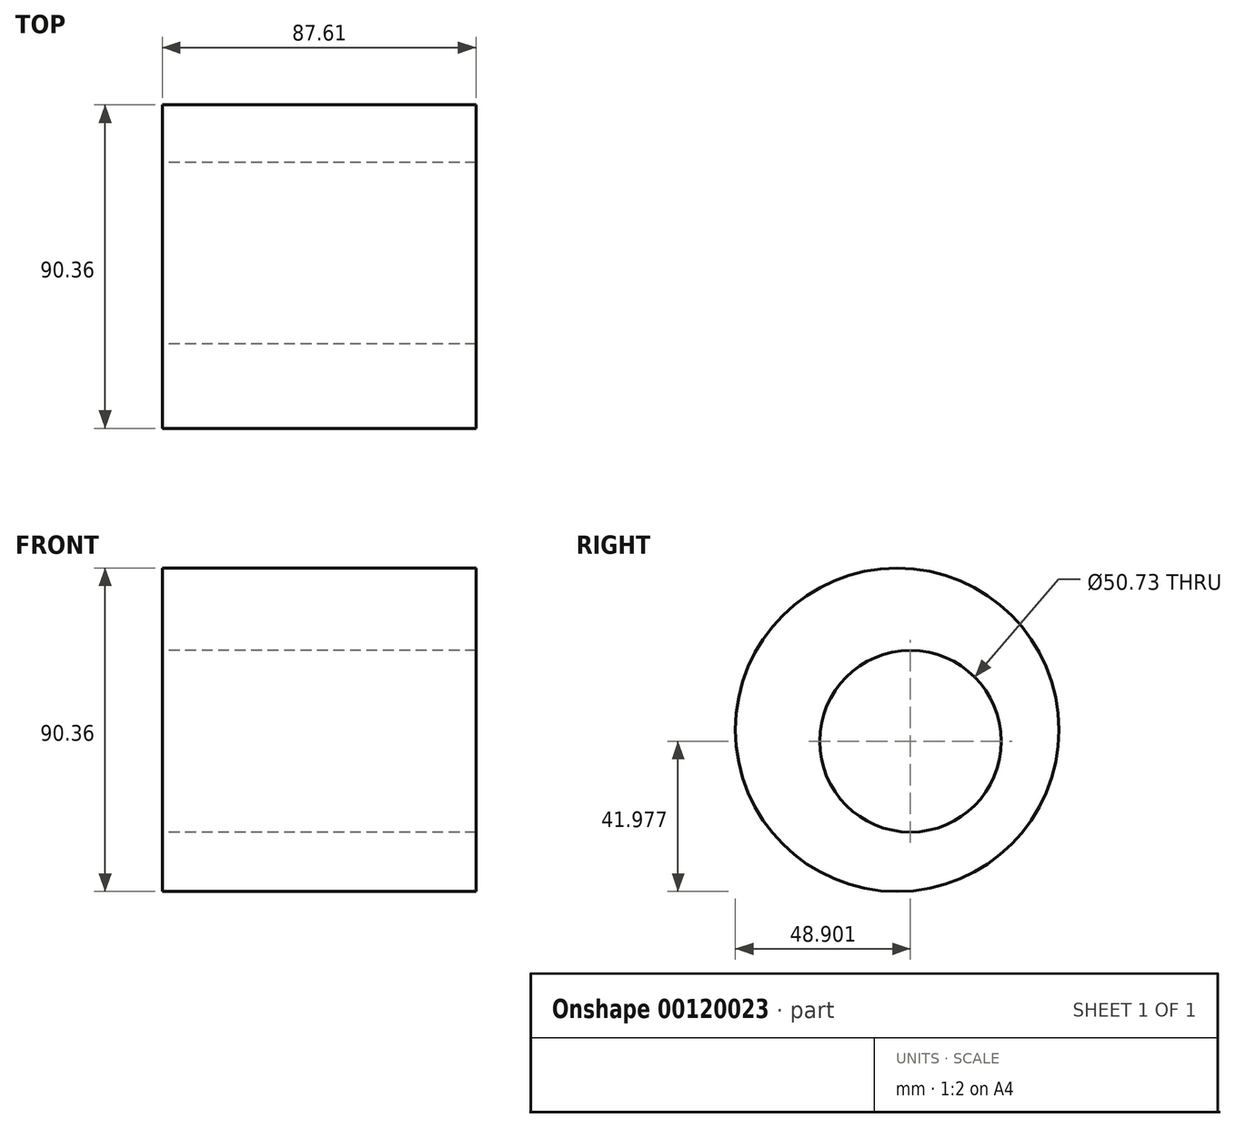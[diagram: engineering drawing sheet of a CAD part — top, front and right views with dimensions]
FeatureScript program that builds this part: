
annotation { "Feature Type Name" : "Feature", "Feature Type Description" : "" }
export const myFeature = defineFeature(function(context is Context, id is Id, definition is map)
    precondition{}
    {
        {
            var Q0;
            Q0=qCreatedBy(makeId("Right.planeOp"),FACE);
            var sketch = newSketch(context, id + "F0", { "sketchPlane" : qUnion([Q0])});
            skCircle(sketch, "E0", {"center": v(0, 0) * mm, "radius": 45.18 * mm});
            skCircle(sketch, "E1", {"center": v(3.72, -3.2) * mm, "radius": 25.36 * mm});
            skSolve(sketch);
        }
        {
            var Q0;
            Q0=makeQuery(id+"F0.imprint","IMPRINT",FACE,{"disambiguationData":[TD([[makeQuery(id+"F0.imprint","IMPRINT",EDGE,{"derivedFrom":sQuery(id+"F0.wireOp",EDGE,"E0")}),1.0]])]});
            extrude(context, id + "F1", {"entities" : qUnion([Q0]), "depth" : 87.61 * mm});
        }
    });
